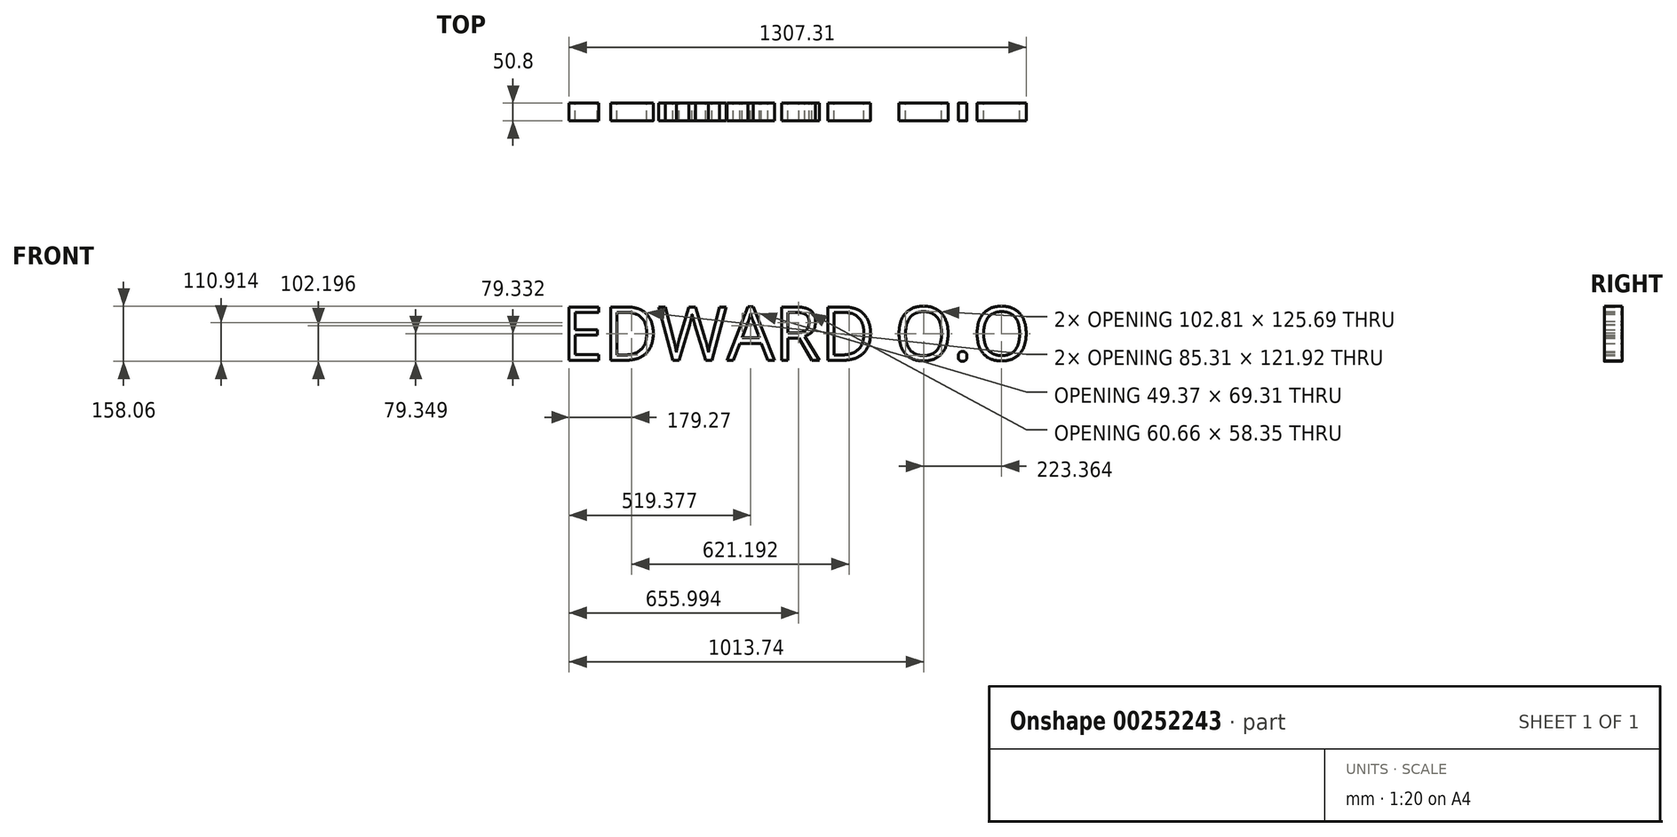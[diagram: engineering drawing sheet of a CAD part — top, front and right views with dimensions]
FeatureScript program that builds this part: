
annotation { "Feature Type Name" : "Feature", "Feature Type Description" : "" }
export const myFeature = defineFeature(function(context is Context, id is Id, definition is map)
    precondition{}
    {
        {
            var Q0;
            Q0=qCreatedBy(makeId("Front.planeOp"),FACE);
            var sketch = newSketch(context, id + "F0", { "sketchPlane" : qUnion([Q0])});
            skText(sketch, "E0", { "text": "EDWARD O.O", "fontName": "OpenSans-Regular.ttf"});
            const initialGuessF0  = {"E0": [-0.12765, -0.0791, 1, 0, 0.15392]};
            skSetInitialGuess(sketch, initialGuessF0);
            skSolve(sketch);
        }
        {
            var Q0;
            Q0 = qSketchRegion(id + "F0", true);
            extrude(context, id + "F1", {"entities" : qUnion([Q0]), "depth" : 50.8 * mm});
        }
    });
